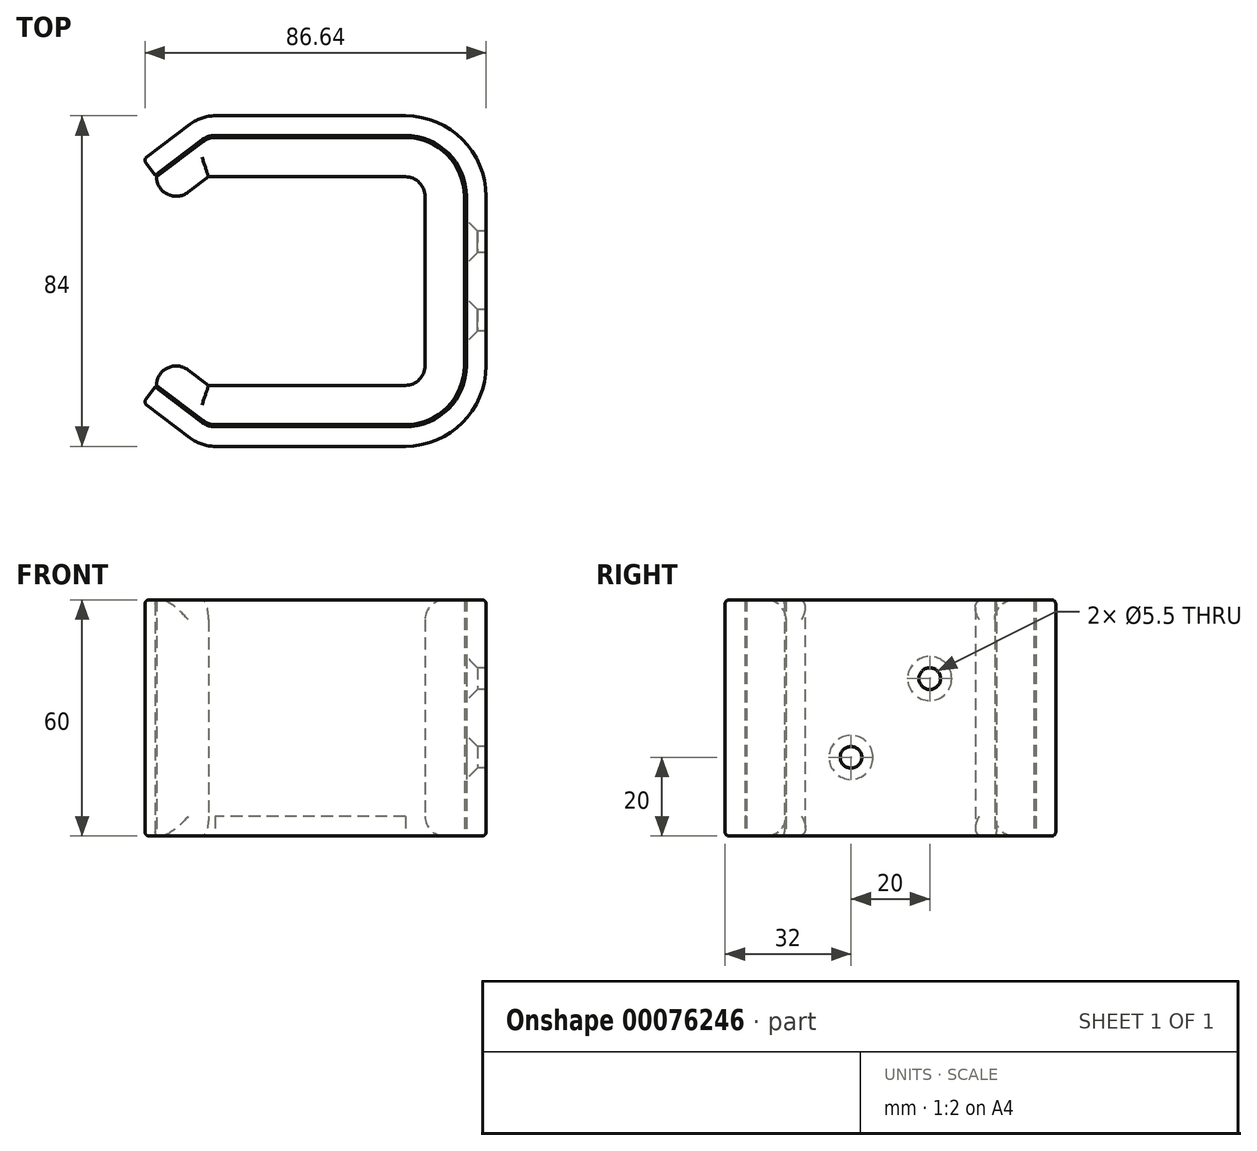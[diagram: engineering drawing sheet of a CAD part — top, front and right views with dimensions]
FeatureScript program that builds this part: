
annotation { "Feature Type Name" : "Feature", "Feature Type Description" : "" }
export const myFeature = defineFeature(function(context is Context, id is Id, definition is map)
    precondition{}
    {
        {
            var Q0;
            Q0=qCreatedBy(makeId("Top.planeOp"),FACE);
            var sketch = newSketch(context, id + "F0", { "sketchPlane" : qUnion([Q0])});
            skLineSegment(sketch, "E0.bottom", {"start": v(22.5, -26.5) * mm, "end": v(-27.5, -26.5) * mm});
            skLineSegment(sketch, "E0.top", {"start": v(22.5, 26.5) * mm, "end": v(-27.5, 26.5) * mm});
            skLineSegment(sketch, "E0.left", {"start": v(27.5, -21.5) * mm, "end": v(27.5, 21.5) * mm});
            skPoint(sketch, "E0.middle", {"position": v(0, 0) * mm});
            skPoint(sketch, "E1.visualSharp", {"position": v(27.5, 26.5) * mm});
            skArc(sketch, "E1.filletArc", {"start": v(27.5, 21.5) * mm, "mid": v(26.04, 25.04) * mm, "end": v(22.5, 26.5) * mm});
            skPoint(sketch, "E2.visualSharp", {"position": v(27.5, -26.5) * mm});
            skArc(sketch, "E2.filletArc", {"start": v(22.5, -26.5) * mm, "mid": v(26.04, -25.04) * mm, "end": v(27.5, -21.5) * mm});
            skLineSegment(sketch, "E3.0", {"start": v(22.5, 36.5) * mm, "end": v(-25.82, 36.5) * mm});
            skLineSegment(sketch, "E3.1", {"start": v(22.5, -36.5) * mm, "end": v(-25.82, -36.5) * mm});
            skArc(sketch, "E3.2", {"start": v(22.5, -36.5) * mm, "mid": v(33.1, -32.1) * mm, "end": v(37.5, -21.5) * mm});
            skLineSegment(sketch, "E3.3", {"start": v(37.5, -21.5) * mm, "end": v(37.5, 21.5) * mm});
            skArc(sketch, "E3.4", {"start": v(37.5, 21.5) * mm, "mid": v(33.1, 32.1) * mm, "end": v(22.5, 36.5) * mm});
            skLineSegment(sketch, "E4", {"start": v(-40.73, 26.5) * mm, "end": v(-28.84, 35.49) * mm});
            skLineSegment(sketch, "E5.MirrorCS", {"start": v(-40.73, -26.5) * mm, "end": v(-28.84, -35.49) * mm});
            skPoint(sketch, "E6.visualSharp", {"position": v(-27.5, 36.5) * mm});
            skArc(sketch, "E6.filletArc", {"start": v(-25.82, 36.5) * mm, "mid": v(-27.41, 36.24) * mm, "end": v(-28.84, 35.49) * mm});
            skPoint(sketch, "E7.visualSharp", {"position": v(-27.5, -36.5) * mm});
            skArc(sketch, "E7.filletArc", {"start": v(-28.84, -35.49) * mm, "mid": v(-27.41, -36.24) * mm, "end": v(-25.82, -36.5) * mm});
            skLineSegment(sketch, "E8", {"start": v(-27.5, 26.5) * mm, "end": v(-40.73, 16.5) * mm});
            skLineSegment(sketch, "E9", {"start": v(-40.73, 16.5) * mm, "end": v(-40.73, 26.5) * mm});
            skLineSegment(sketch, "E10", {"start": v(-27.5, -26.5) * mm, "end": v(-40.73, -16.5) * mm});
            skLineSegment(sketch, "E11", {"start": v(-40.73, -16.5) * mm, "end": v(-40.73, -26.5) * mm});
            skSolve(sketch);
        }
        {
            var Q0;
            Q0 = qSketchRegion(id + "F0", true);
            extrude(context, id + "F1", {"entities" : qUnion([Q0]), "depth" : 60 * mm});
        }
        {
            var Q0;
            Q0=qCreatedBy(makeId("Top.planeOp"),FACE);
            var sketch = newSketch(context, id + "F2", { "sketchPlane" : qUnion([Q0])});
            skLineSegment(sketch, "E12.0", {"start": v(-40.73, 26.5) * mm, "end": v(-28.84, 35.49) * mm});
            skArc(sketch, "E13.0", {"start": v(-25.82, 36.5) * mm, "mid": v(-27.41, 36.24) * mm, "end": v(-28.84, 35.49) * mm});
            skLineSegment(sketch, "E14.0", {"start": v(22.5, 36.5) * mm, "end": v(-25.82, 36.5) * mm});
            skArc(sketch, "E15.0", {"start": v(37.5, 21.5) * mm, "mid": v(33.1, 32.1) * mm, "end": v(22.5, 36.5) * mm});
            skLineSegment(sketch, "E16.0", {"start": v(37.5, -21.5) * mm, "end": v(37.5, 21.5) * mm});
            skArc(sketch, "E17.0", {"start": v(22.5, -36.5) * mm, "mid": v(33.1, -32.1) * mm, "end": v(37.5, -21.5) * mm});
            skLineSegment(sketch, "E18.0", {"start": v(22.5, -36.5) * mm, "end": v(-25.82, -36.5) * mm});
            skArc(sketch, "E19.0", {"start": v(-28.84, -35.49) * mm, "mid": v(-27.41, -36.24) * mm, "end": v(-25.82, -36.5) * mm});
            skLineSegment(sketch, "E20.0", {"start": v(-40.73, -26.5) * mm, "end": v(-28.84, -35.49) * mm});
            skLineSegment(sketch, "E21.0", {"start": v(-41.03, -26.9) * mm, "end": v(-29.14, -35.89) * mm});
            skArc(sketch, "E21.1", {"start": v(-29.14, -35.89) * mm, "mid": v(-27.57, -36.71) * mm, "end": v(-25.82, -37) * mm});
            skLineSegment(sketch, "E21.2", {"start": v(22.5, -37) * mm, "end": v(-25.82, -37) * mm});
            skArc(sketch, "E21.3", {"start": v(22.5, -37) * mm, "mid": v(33.46, -32.46) * mm, "end": v(38, -21.5) * mm});
            skLineSegment(sketch, "E21.4", {"start": v(38, -21.5) * mm, "end": v(38, 21.5) * mm});
            skLineSegment(sketch, "E21.5", {"start": v(-41.03, 26.9) * mm, "end": v(-29.14, 35.89) * mm});
            skArc(sketch, "E21.6", {"start": v(-25.82, 37) * mm, "mid": v(-27.57, 36.71) * mm, "end": v(-29.14, 35.89) * mm});
            skLineSegment(sketch, "E21.7", {"start": v(22.5, 37) * mm, "end": v(-25.82, 37) * mm});
            skArc(sketch, "E21.8", {"start": v(38, 21.5) * mm, "mid": v(33.46, 32.46) * mm, "end": v(22.5, 37) * mm});
            skLineSegment(sketch, "E22.0", {"start": v(-43.25, -31.5) * mm, "end": v(-32.15, -39.88) * mm});
            skArc(sketch, "E22.1", {"start": v(-32.15, -39.88) * mm, "mid": v(-29.16, -41.45) * mm, "end": v(-25.82, -42) * mm});
            skLineSegment(sketch, "E22.2", {"start": v(22.5, -42) * mm, "end": v(-25.82, -42) * mm});
            skArc(sketch, "E22.3", {"start": v(22.5, -42) * mm, "mid": v(37, -36) * mm, "end": v(43, -21.5) * mm});
            skLineSegment(sketch, "E22.4", {"start": v(43, -21.5) * mm, "end": v(43, 21.5) * mm});
            skLineSegment(sketch, "E22.5", {"start": v(-43.25, 31.5) * mm, "end": v(-32.15, 39.88) * mm});
            skArc(sketch, "E22.6", {"start": v(-25.82, 42) * mm, "mid": v(-29.16, 41.45) * mm, "end": v(-32.15, 39.88) * mm});
            skLineSegment(sketch, "E22.7", {"start": v(22.5, 42) * mm, "end": v(-25.82, 42) * mm});
            skArc(sketch, "E22.8", {"start": v(43, 21.5) * mm, "mid": v(37, 36) * mm, "end": v(22.5, 42) * mm});
            skLineSegment(sketch, "E23", {"start": v(-43.44, 30.09) * mm, "end": v(-41.03, 26.9) * mm});
            skLineSegment(sketch, "E24", {"start": v(-43.44, -30.09) * mm, "end": v(-41.03, -26.9) * mm});
            skPoint(sketch, "E25.visualSharp", {"position": v(-44.04, 30.89) * mm});
            skArc(sketch, "E25.filletArc", {"start": v(-43.25, 31.5) * mm, "mid": v(-43.63, 30.83) * mm, "end": v(-43.44, 30.09) * mm});
            skPoint(sketch, "E26.visualSharp", {"position": v(-44.04, -30.89) * mm});
            skArc(sketch, "E26.filletArc", {"start": v(-43.44, -30.09) * mm, "mid": v(-43.63, -30.83) * mm, "end": v(-43.25, -31.5) * mm});
            skSolve(sketch);
        }
        {
            var Q0;
            Q0=makeQuery(id+"F1.opExtrude","CAP_FACE",FACE,{"disambiguationData":[OSD([sQuery(id+"F0.wireOp",EDGE,"E0.bottom"),sQuery(id+"F0.wireOp",EDGE,"E0.top"),sQuery(id+"F0.wireOp",EDGE,"E0.left"),sQuery(id+"F0.wireOp",EDGE,"E1.filletArc"),sQuery(id+"F0.wireOp",EDGE,"E2.filletArc"),sQuery(id+"F0.wireOp",EDGE,"E3.0"),sQuery(id+"F0.wireOp",EDGE,"E3.1"),sQuery(id+"F0.wireOp",EDGE,"E3.2"),sQuery(id+"F0.wireOp",EDGE,"E3.3"),sQuery(id+"F0.wireOp",EDGE,"E3.4"),sQuery(id+"F0.wireOp",EDGE,"E4"),sQuery(id+"F0.wireOp",EDGE,"E5.MirrorCS"),sQuery(id+"F0.wireOp",EDGE,"E6.filletArc"),sQuery(id+"F0.wireOp",EDGE,"E7.filletArc"),sQuery(id+"F0.wireOp",EDGE,"E8"),sQuery(id+"F0.wireOp",EDGE,"E9"),sQuery(id+"F0.wireOp",EDGE,"E10"),sQuery(id+"F0.wireOp",EDGE,"E11")])],"isStart":true});
            var sketch = newSketch(context, id + "F3", { "sketchPlane" : qUnion([Q0])});
            skLineSegment(sketch, "E27.0", {"start": v(-25.82, 32) * mm, "end": v(-25.82, 37) * mm});
            skLineSegment(sketch, "E28.0", {"start": v(22.5, 32) * mm, "end": v(-25.82, 32) * mm});
            skLineSegment(sketch, "E29.0", {"start": v(22.5, 32) * mm, "end": v(22.5, 37) * mm});
            skLineSegment(sketch, "E30.0", {"start": v(22.5, -32) * mm, "end": v(22.5, -37) * mm});
            skLineSegment(sketch, "E31.0", {"start": v(22.5, -32) * mm, "end": v(-25.82, -32) * mm});
            skLineSegment(sketch, "E32.0", {"start": v(-25.82, -32) * mm, "end": v(-25.82, -37) * mm});
            skLineSegment(sketch, "E33.bottom", {"start": v(-25.82, 32) * mm, "end": v(22.5, 32) * mm});
            skLineSegment(sketch, "E33.top", {"start": v(-25.82, 36.5) * mm, "end": v(22.5, 36.5) * mm});
            skLineSegment(sketch, "E33.left", {"start": v(-25.82, 32) * mm, "end": v(-25.82, 36.5) * mm});
            skLineSegment(sketch, "E33.right", {"start": v(22.5, 32) * mm, "end": v(22.5, 36.5) * mm});
            skLineSegment(sketch, "E34.bottom", {"start": v(-25.82, -32) * mm, "end": v(22.5, -32) * mm});
            skLineSegment(sketch, "E34.top", {"start": v(-25.82, -36.5) * mm, "end": v(22.5, -36.5) * mm});
            skLineSegment(sketch, "E34.left", {"start": v(-25.82, -32) * mm, "end": v(-25.82, -36.5) * mm});
            skLineSegment(sketch, "E34.right", {"start": v(22.5, -32) * mm, "end": v(22.5, -36.5) * mm});
            skSolve(sketch);
        }
        {
            var Q0;
            Q0 = qSketchRegion(id + "F3", true);
            extrude(context, id + "F4", {"entities" : qUnion([Q0]), "operationType" : NewBodyOperationType.REMOVE, "oppositeDirection" : true, "depth" : 5 * mm});
        }
        {
            var Q0;
            Q0=makeQuery(id+"F2.imprint","IMPRINT",FACE,{"disambiguationData":[TD([[makeQuery(id+"F2.imprint","IMPRINT",EDGE,{"derivedFrom":sQuery(id+"F2.wireOp",EDGE,"E21.0")}),-1.0]])]});
            extrude(context, id + "F5", {"entities" : qUnion([Q0]), "depth" : 60 * mm});
        }
        {
            var Q0;
            Q0=makeQuery(id+"F1.opExtrude","CAP_EDGE",EDGE,{"disambiguationData":[OSD([sQuery(id+"F0.wireOp",EDGE,"E8")])],"isStart":false});
            var Q1;
            Q1=makeQuery(id+"F1.opExtrude","CAP_EDGE",EDGE,{"disambiguationData":[OSD([sQuery(id+"F0.wireOp",EDGE,"E0.top")])],"isStart":false});
            var Q2;
            Q2=makeQuery(id+"F1.opExtrude","CAP_EDGE",EDGE,{"disambiguationData":[OSD([sQuery(id+"F0.wireOp",EDGE,"E10")])],"isStart":false});
            var Q3;
            Q3=makeQuery(id+"F1.opExtrude","SWEPT_EDGE",EDGE,{"disambiguationData":[OSD([sQuery(id+"F0.wireOp",EDGE,"E8"),sQuery(id+"F0.wireOp",EDGE,"E9")])]});
            var Q4;
            Q4=makeQuery(id+"F1.opExtrude","SWEPT_EDGE",EDGE,{"disambiguationData":[OSD([sQuery(id+"F0.wireOp",EDGE,"E10"),sQuery(id+"F0.wireOp",EDGE,"E11")])]});
            var Q5;
            Q5=makeQuery(id+"F1.opExtrude","CAP_EDGE",EDGE,{"disambiguationData":[OSD([sQuery(id+"F0.wireOp",EDGE,"E8")])],"isStart":true});
            var Q6;
            Q6=makeQuery(id+"F1.opExtrude","CAP_EDGE",EDGE,{"disambiguationData":[OSD([sQuery(id+"F0.wireOp",EDGE,"E10")])],"isStart":true});
            var Q7;
            Q7=makeQuery(id+"F1.opExtrude","CAP_EDGE",EDGE,{"disambiguationData":[OSD([sQuery(id+"F0.wireOp",EDGE,"E0.bottom")])],"isStart":true});
            fillet(context, id + "F6", {"entities" : qUnion([Q0, Q1, Q2, Q3, Q4, Q5, Q6, Q7]), "radius" : 5 * mm, "tangentPropagation" : true, "allowEdgeOverflow" : false});
        }
        {
            var Q0;
            Q0=makeQuery(id+"F5.opExtrude","SWEPT_FACE",FACE,{"disambiguationData":[OSD([sQuery(id+"F2.wireOp",EDGE,"E21.4")])]});
            var sketch = newSketch(context, id + "F7", { "sketchPlane" : qUnion([Q0])});
            skCircle(sketch, "E35", {"center": v(-10, 40) * mm, "radius": 3 * mm});
            skCircle(sketch, "E36", {"center": v(10, 20) * mm, "radius": 3 * mm});
            skSolve(sketch);
        }
        {
            var Q0;
            Q0=sQuery(id+"F7.wireOp",VERTEX,"E35.center");
            var Q1;
            Q1=sQuery(id+"F7.wireOp",VERTEX,"E36.center");
            var Q2;
            Q2=makeQuery(id+"F5.opExtrude","SWEPT_BODY",BODY,{"disambiguationData":[OSD([sQuery(id+"F2.wireOp",EDGE,"E21.0"),sQuery(id+"F2.wireOp",EDGE,"E21.1"),sQuery(id+"F2.wireOp",EDGE,"E21.2"),sQuery(id+"F2.wireOp",EDGE,"E21.3"),sQuery(id+"F2.wireOp",EDGE,"E21.4"),sQuery(id+"F2.wireOp",EDGE,"E21.5"),sQuery(id+"F2.wireOp",EDGE,"E21.6"),sQuery(id+"F2.wireOp",EDGE,"E21.7"),sQuery(id+"F2.wireOp",EDGE,"E21.8"),sQuery(id+"F2.wireOp",EDGE,"E22.0"),sQuery(id+"F2.wireOp",EDGE,"E22.1"),sQuery(id+"F2.wireOp",EDGE,"E22.2"),sQuery(id+"F2.wireOp",EDGE,"E22.3"),sQuery(id+"F2.wireOp",EDGE,"E22.4"),sQuery(id+"F2.wireOp",EDGE,"E22.5"),sQuery(id+"F2.wireOp",EDGE,"E22.6"),sQuery(id+"F2.wireOp",EDGE,"E22.7"),sQuery(id+"F2.wireOp",EDGE,"E22.8"),sQuery(id+"F2.wireOp",EDGE,"E23"),sQuery(id+"F2.wireOp",EDGE,"E24"),sQuery(id+"F2.wireOp",EDGE,"E25.filletArc"),sQuery(id+"F2.wireOp",EDGE,"E26.filletArc")])]});
            hole(context, id + "F8", {"style" : HoleStyle.C_SINK, "endStyle" : HoleEndStyle.BLIND, "standardTappedOrClearance" : lookupTablePath({ "standard" : "ISO", "fit" : "Normal", "size" : "M5", "type" : "Clearance" }), "standardBlindInLast" : lookupTablePath({ "fit" : "Standard", "standard" : "ISO", "size" : "M5", "type" : "Clearance" }), "holeDiameter" : 5.5 * mm, "cSinkDiameter" : 11.2 * mm, "cSinkAngle" : 90 * degree, "holeDepth" : 12 * mm, "startFromSketch" : true, "locations" : qUnion([Q0, Q1]), "scope" : qUnion([Q2])});
        }
        {
            var Q0;
            Q0=makeQuery(id+"F5.opExtrude","SWEPT_FACE",FACE,{"disambiguationData":[OSD([sQuery(id+"F2.wireOp",EDGE,"E21.7")])]});
            var sketch = newSketch(context, id + "F9", { "sketchPlane" : qUnion([Q0])});
            skLineSegment(sketch, "E37.bottom", {"start": v(22.5, 0) * mm, "end": v(-25.82, 0) * mm});
            skLineSegment(sketch, "E37.top", {"start": v(22.5, 5) * mm, "end": v(-25.82, 5) * mm});
            skLineSegment(sketch, "E37.left", {"start": v(22.5, 0) * mm, "end": v(22.5, 5) * mm});
            skLineSegment(sketch, "E37.right", {"start": v(-25.82, 0) * mm, "end": v(-25.82, 5) * mm});
            skSolve(sketch);
        }
        {
            var Q0;
            Q0 = qSketchRegion(id + "F9", true);
            var Q1;
            Q1=makeQuery(id+"F9.imprint","IMPRINT",FACE,{"disambiguationData":[TD([[makeQuery(id+"F9.imprint","IMPRINT",EDGE,{"derivedFrom":sQuery(id+"F9.wireOp",EDGE,"E37.bottom")}),-1.0]])]});
            extrude(context, id + "F10", {"entities" : qUnion([Q0, Q1]), "operationType" : NewBodyOperationType.ADD, "depth" : 5 * mm});
        }
        {
            var Q0;
            Q0=makeQuery(id+"F5.opExtrude","SWEPT_FACE",FACE,{"disambiguationData":[OSD([sQuery(id+"F2.wireOp",EDGE,"E21.2")])]});
            var sketch = newSketch(context, id + "F11", { "sketchPlane" : qUnion([Q0])});
            skLineSegment(sketch, "E38.bottom", {"start": v(-22.5, 0) * mm, "end": v(25.82, 0) * mm});
            skLineSegment(sketch, "E38.top", {"start": v(-22.5, 5) * mm, "end": v(25.82, 5) * mm});
            skLineSegment(sketch, "E38.left", {"start": v(-22.5, 0) * mm, "end": v(-22.5, 5) * mm});
            skLineSegment(sketch, "E38.right", {"start": v(25.82, 0) * mm, "end": v(25.82, 5) * mm});
            skSolve(sketch);
        }
        {
            var Q0;
            Q0 = qSketchRegion(id + "F11", true);
            extrude(context, id + "F12", {"entities" : qUnion([Q0]), "operationType" : NewBodyOperationType.ADD, "depth" : 5 * mm});
        }
        {
            var Q0;
            Q0=makeQuery(id+"F5.opExtrude","CAP_EDGE",EDGE,{"disambiguationData":[OSD([sQuery(id+"F2.wireOp",EDGE,"E22.7")])],"isStart":false});
            var Q1;
            Q1=makeQuery(id+"F5.opExtrude","CAP_EDGE",EDGE,{"disambiguationData":[OSD([sQuery(id+"F2.wireOp",EDGE,"E22.5")])],"isStart":true});
            fillet(context, id + "F13", {"entities" : qUnion([Q0, Q1]), "radius" : 1 * mm, "tangentPropagation" : true, "allowEdgeOverflow" : false});
        }
    });
